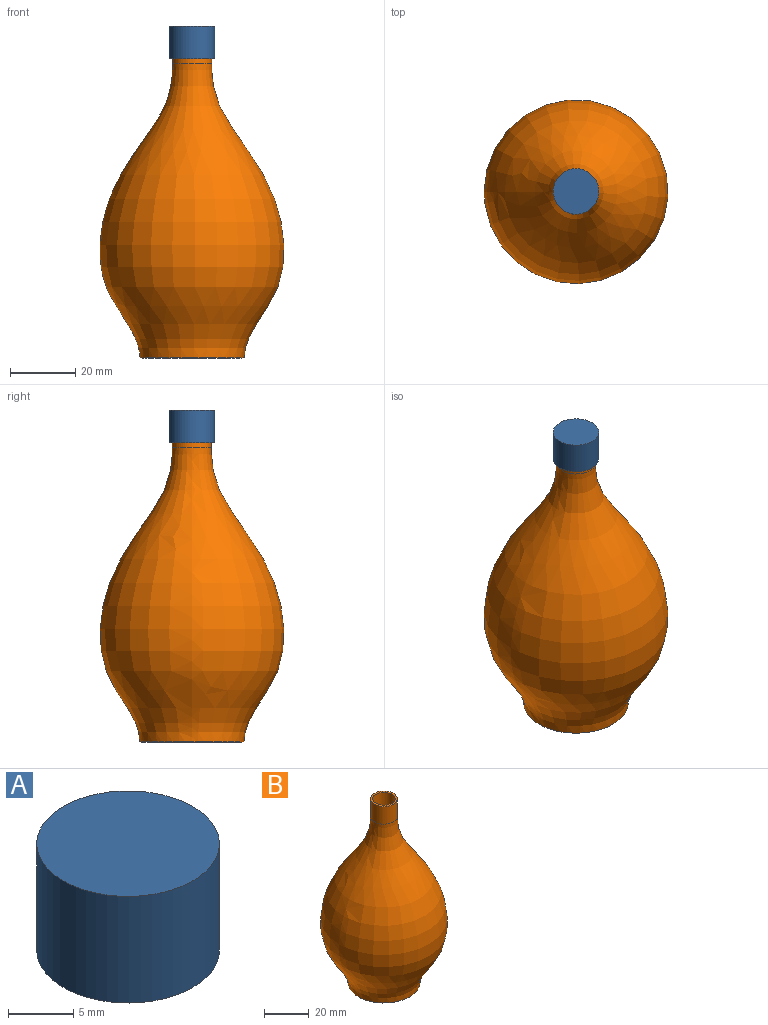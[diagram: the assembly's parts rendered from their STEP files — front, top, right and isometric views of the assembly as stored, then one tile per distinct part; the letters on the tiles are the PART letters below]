
ASSEMBLY  parts=2 mates=1
PART A: 5 faces, bbox 14x14x10 mm
  f0: cylinder r=7mm len=14mm, axis (0,0,-1), area 439.8mm2, adj f1,f2
  f1: plane 14x14mm, normal (0,0,1), area 153.9mm2, adj f0
  f2: plane 14x14mm, normal (0,0,-1), area 31.2mm2, adj f0,f3
  f3: cylinder r=6.25mm len=12.5mm, axis (0,0,-1), area 314.2mm2, adj f2,f4
  f4: plane 12.5x12.5mm, normal (0,0,-1), area 122.7mm2, adj f3
PART B: 8 faces, bbox 56.5x56.5x100 mm
  f0: revolved ~89.44x54.57mm, area 11323.9mm2, adj f1,f7
  f1: plane 30.1x30.1mm, normal (0,0,1), area 711.7mm2, adj f0
  f2: plane 30.68x30.68mm, normal (0,0,-1), area 739.4mm2, adj f3
  f3: cone r=16mm half-angle=89.9deg, axis (0,0,1), area 65mm2, adj f2,f4
  f4: revolved ~90.44x56.52mm, area 12087.5mm2, adj f3,f5
  f5: cylinder r=6mm len=12mm, axis (0,0,-1), area 360.5mm2, adj f4,f6
  f6: plane 12x12mm, normal (0,0,1), area 34.6mm2, adj f5,f7
  f7: cylinder r=5mm len=10mm, axis (0,0,-1), area 300.4mm2, adj f0,f6
PLACE A t=(-17.12,-16.4,32.22)mm
PLACE B t=(-17.12,-16.4,1.2)mm fixed
MATE cylindrical A.f3 <-> B.f3  axis (0,0,-1) through (-17.12,-16.4,40.22)mm
